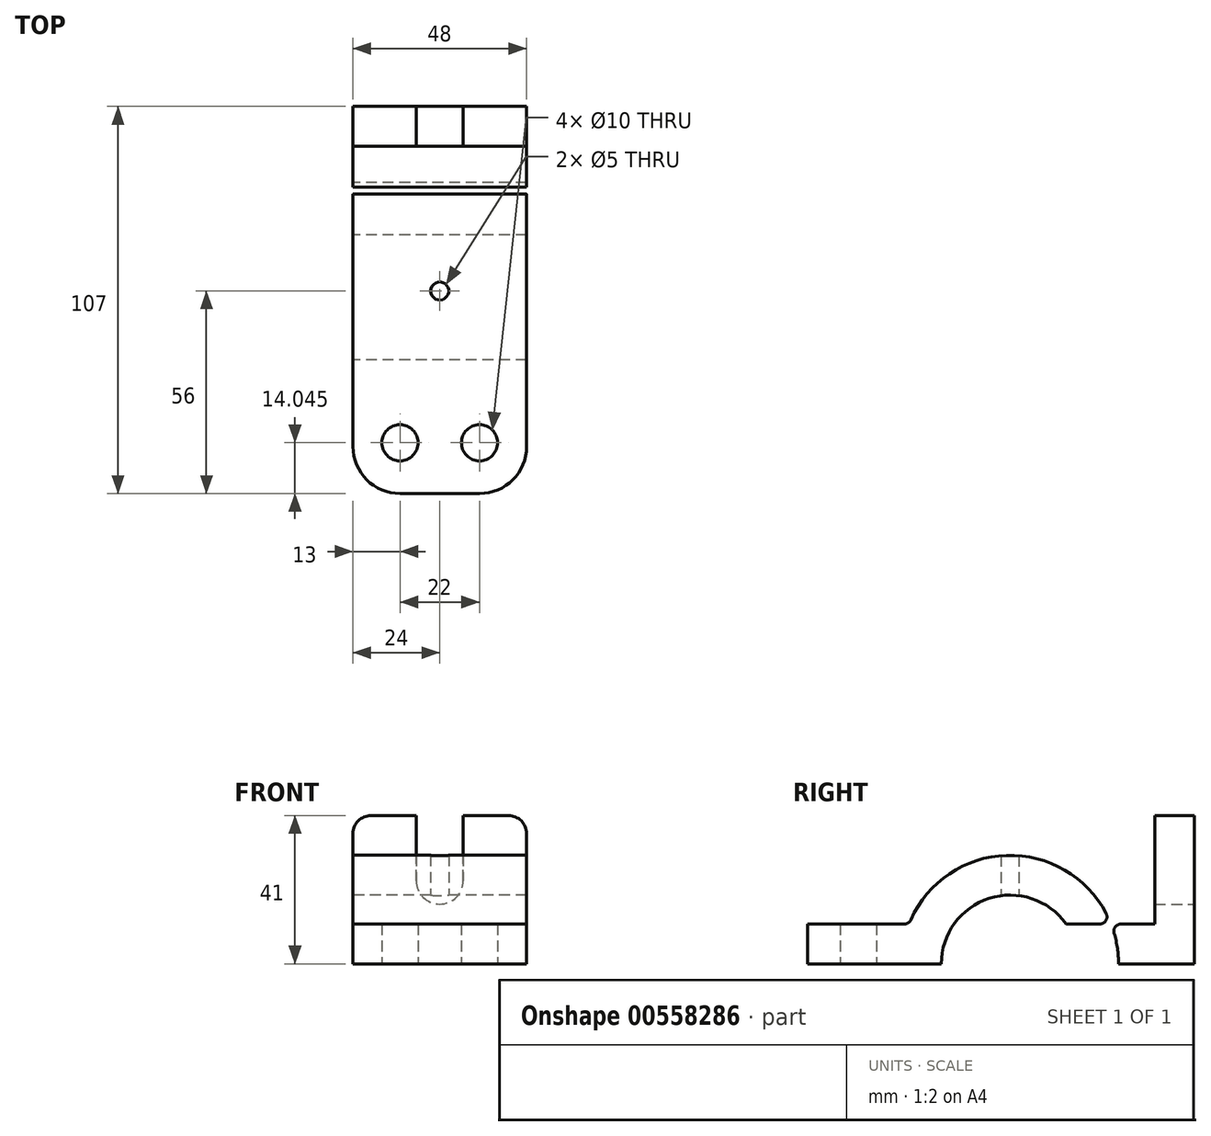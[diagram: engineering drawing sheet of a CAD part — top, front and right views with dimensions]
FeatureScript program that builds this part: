
annotation { "Feature Type Name" : "Feature", "Feature Type Description" : "" }
export const myFeature = defineFeature(function(context is Context, id is Id, definition is map)
    precondition{}
    {
        {
            var Q0;
            Q0=qCreatedBy(makeId("Right.planeOp"),FACE);
            var sketch = newSketch(context, id + "F0", { "sketchPlane" : qUnion([Q0])});
            skCircle(sketch, "E0", {"center": v(0, 0) * mm, "radius": 19 * mm});
            skCircle(sketch, "E1", {"center": v(0, 0) * mm, "radius": 30 * mm});
            skLineSegment(sketch, "E2.bottom", {"start": v(-56, 0) * mm, "end": v(51, 0) * mm});
            skLineSegment(sketch, "E2.top", {"start": v(-56, 11) * mm, "end": v(51, 11) * mm});
            skLineSegment(sketch, "E2.left", {"start": v(-56, 0) * mm, "end": v(-56, 11) * mm});
            skLineSegment(sketch, "E2.right", {"start": v(51, 0) * mm, "end": v(51, 11) * mm});
            skLineSegment(sketch, "E3.bottom", {"start": v(51, 41) * mm, "end": v(40, 41) * mm});
            skLineSegment(sketch, "E3.top", {"start": v(51, 11) * mm, "end": v(40, 11) * mm});
            skLineSegment(sketch, "E3.left", {"start": v(51, 41) * mm, "end": v(51, 11) * mm});
            skLineSegment(sketch, "E3.right", {"start": v(40, 41) * mm, "end": v(40, 11) * mm});
            skSolve(sketch);
        }
        {
            var Q0;
            Q0=makeQuery(id+"F0.imprint","IMPRINT",FACE,{"disambiguationData":[TD([[makeQuery(id+"F0.imprint","IMPRINT",EDGE,{"derivedFrom":sQuery(id+"F0.wireOp",EDGE,"E3.bottom")}),1.0]])]});
            var Q1;
            {var subQ4=sQuery(id+"F0.wireOp",EDGE,"E2.right");Q1=makeQuery(id+"F0.imprint","IMPRINT",FACE,{"disambiguationData":[TD([[makeQuery(id+"F0.imprint","IMPRINT",EDGE,{"derivedFrom":subQ4}),1.0]])]});}
            var Q2;
            {var subQ0=sQuery(id+"F0.wireOp",EDGE,"E2.top");var subQ1=sQuery(id+"F0.wireOp",EDGE,"E0");var subQ2=makeQuery(id+"F0.imprint","INTERSECT",VERTEX,{"disambiguationData":[OD(0.0)],"derivedFrom":[subQ1,subQ0]});Q2=makeQuery(id+"F0.imprint","IMPRINT",FACE,{"disambiguationData":[TD([[makeQuery(id+"F0.imprint","IMPRINT",EDGE,{"disambiguationData":[TD([[subQ2,-1.0]])],"derivedFrom":subQ1}),-1.0]])]});}
            var Q3;
            {var subQ0=sQuery(id+"F0.wireOp",EDGE,"E2.top");var subQ1=sQuery(id+"F0.wireOp",EDGE,"E0");var subQ2=makeQuery(id+"F0.imprint","INTERSECT",VERTEX,{"disambiguationData":[OD(0.0)],"derivedFrom":[subQ1,subQ0]});Q3=makeQuery(id+"F0.imprint","IMPRINT",FACE,{"disambiguationData":[TD([[makeQuery(id+"F0.imprint","IMPRINT",EDGE,{"disambiguationData":[TD([[subQ2,1.0]])],"derivedFrom":subQ1}),-1.0]])]});}
            var Q4;
            {var subQ0=sQuery(id+"F0.wireOp",EDGE,"E2.top");var subQ1=sQuery(id+"F0.wireOp",EDGE,"E0");var subQ2=makeQuery(id+"F0.imprint","INTERSECT",VERTEX,{"disambiguationData":[OD(1.0)],"derivedFrom":[subQ1,subQ0]});Q4=makeQuery(id+"F0.imprint","IMPRINT",FACE,{"disambiguationData":[TD([[makeQuery(id+"F0.imprint","IMPRINT",EDGE,{"disambiguationData":[TD([[subQ2,-1.0]])],"derivedFrom":subQ1}),-1.0]])]});}
            var Q5;
            {var subQ5=sQuery(id+"F0.wireOp",EDGE,"E2.left");Q5=makeQuery(id+"F0.imprint","IMPRINT",FACE,{"disambiguationData":[TD([[makeQuery(id+"F0.imprint","IMPRINT",EDGE,{"derivedFrom":subQ5}),-1.0]])]});}
            extrude(context, id + "F1", {"entities" : qUnion([Q0, Q1, Q2, Q3, Q4, Q5]), "endBound" : BoundingType.SYMMETRIC, "depth" : 48 * mm, "offsetDistance" : 25 * mm});
        }
        {
            var Q0;
            Q0=makeQuery(id+"F1.opExtrude","SWEPT_FACE",FACE,{"disambiguationData":[OSD([sQuery(id+"F0.wireOp",EDGE,"E2.right"),sQuery(id+"F0.wireOp",EDGE,"E3.left")])]});
            var sketch = newSketch(context, id + "F2", { "sketchPlane" : qUnion([Q0])});
            skLineSegment(sketch, "E4", {"start": v(0, 0) * mm, "end": v(0, 41) * mm});
            skCircle(sketch, "E5", {"center": v(0, 23) * mm, "radius": 6.5 * mm});
            skLineSegment(sketch, "E6", {"start": v(-6.5, 23) * mm, "end": v(-6.5, 41) * mm});
            skLineSegment(sketch, "E7", {"start": v(6.5, 23) * mm, "end": v(6.5, 41) * mm});
            skSolve(sketch);
        }
        {
            var Q0;
            {var subQ5=sQuery(id+"F2.wireOp",EDGE,"E6");Q0=makeQuery(id+"F2.imprint","IMPRINT",FACE,{"disambiguationData":[TD([[makeQuery(id+"F2.imprint","IMPRINT",EDGE,{"derivedFrom":subQ5}),-1.0]])]});}
            var Q1;
            {var subQ0=sQuery(id+"F2.wireOp",EDGE,"E5");var subQ1=sQuery(id+"F2.wireOp",EDGE,"E4");var subQ2=makeQuery(id+"F2.imprint","INTERSECT",VERTEX,{"disambiguationData":[OD(0.0)],"derivedFrom":[subQ1,subQ0]});Q1=makeQuery(id+"F2.imprint","IMPRINT",FACE,{"disambiguationData":[TD([[makeQuery(id+"F2.imprint","IMPRINT",EDGE,{"disambiguationData":[TD([[subQ2,-1.0]])],"derivedFrom":subQ1}),1.0]])]});}
            var Q2;
            {var subQ0=sQuery(id+"F2.wireOp",EDGE,"E5");var subQ1=sQuery(id+"F2.wireOp",EDGE,"E4");var subQ2=makeQuery(id+"F2.imprint","INTERSECT",VERTEX,{"disambiguationData":[OD(0.0)],"derivedFrom":[subQ1,subQ0]});Q2=makeQuery(id+"F2.imprint","IMPRINT",FACE,{"disambiguationData":[TD([[makeQuery(id+"F2.imprint","IMPRINT",EDGE,{"disambiguationData":[TD([[subQ2,-1.0]])],"derivedFrom":subQ1}),-1.0]])]});}
            var Q3;
            {var subQ5=sQuery(id+"F2.wireOp",EDGE,"E7");Q3=makeQuery(id+"F2.imprint","IMPRINT",FACE,{"disambiguationData":[TD([[makeQuery(id+"F2.imprint","IMPRINT",EDGE,{"derivedFrom":subQ5}),1.0]])]});}
            var Q4;
            Q4=makeQuery(id+"F1.opExtrude","SWEPT_FACE",FACE,{"disambiguationData":[OSD([sQuery(id+"F0.wireOp",EDGE,"E3.right")])]});
            extrude(context, id + "F3", {"entities" : qUnion([Q0, Q1, Q2, Q3]), "operationType" : NewBodyOperationType.REMOVE, "endBound" : BoundingType.UP_TO_SURFACE, "oppositeDirection" : true, "depth" : 25 * mm, "endBoundEntityFace" : qUnion([Q4]), "offsetDistance" : 25 * mm});
        }
        {
            var Q0;
            Q0=qCreatedBy(makeId("Top.planeOp"),FACE);
            var sketch = newSketch(context, id + "F4", { "sketchPlane" : qUnion([Q0])});
            skCircle(sketch, "E8", {"center": v(0, 0) * mm, "radius": 2.5 * mm});
            skLineSegment(sketch, "E9", {"start": v(-24, -41.96) * mm, "end": v(24, -41.96) * mm, "construction": true});
            skLineSegment(sketch, "E10", {"start": v(0, -56) * mm, "end": v(0, -27.91) * mm, "construction": true});
            skCircle(sketch, "E11", {"center": v(-11, -41.96) * mm, "radius": 5 * mm});
            skCircle(sketch, "E12", {"center": v(11, -41.96) * mm, "radius": 5 * mm});
            skSolve(sketch);
        }
        {
            var Q0;
            Q0=makeQuery(id+"F4.imprint","IMPRINT",FACE,{"disambiguationData":[TD([[makeQuery(id+"F4.imprint","IMPRINT",EDGE,{"derivedFrom":sQuery(id+"F4.wireOp",EDGE,"E8")}),1.0]])]});
            var Q1;
            Q1=makeQuery(id+"F4.imprint","IMPRINT",FACE,{"disambiguationData":[TD([[makeQuery(id+"F4.imprint","IMPRINT",EDGE,{"derivedFrom":sQuery(id+"F4.wireOp",EDGE,"E12")}),1.0]])]});
            var Q2;
            Q2=makeQuery(id+"F4.imprint","IMPRINT",FACE,{"disambiguationData":[TD([[makeQuery(id+"F4.imprint","IMPRINT",EDGE,{"derivedFrom":sQuery(id+"F4.wireOp",EDGE,"E11")}),1.0]])]});
            extrude(context, id + "F5", {"entities" : qUnion([Q0, Q1, Q2]), "operationType" : NewBodyOperationType.REMOVE, "endBound" : BoundingType.THROUGH_ALL, "depth" : 25 * mm, "offsetDistance" : 25 * mm});
        }
        {
            var Q0;
            Q0=makeQuery(id+"F1.opExtrude","CAP_EDGE",EDGE,{"disambiguationData":[OSD([sQuery(id+"F0.wireOp",EDGE,"E2.left")])],"isStart":true});
            var Q1;
            Q1=makeQuery(id+"F1.opExtrude","CAP_EDGE",EDGE,{"disambiguationData":[OSD([sQuery(id+"F0.wireOp",EDGE,"E2.left")])],"isStart":false});
            fillet(context, id + "F6", {"entities" : qUnion([Q0, Q1]), "radius" : 13 * mm, "tangentPropagation" : true, "allowEdgeOverflow" : false});
        }
        {
            var Q0;
            Q0=makeQuery(id+"F1.opExtrude","CAP_EDGE",EDGE,{"disambiguationData":[OSD([sQuery(id+"F0.wireOp",EDGE,"E3.bottom")])],"isStart":true});
            var Q1;
            Q1=makeQuery(id+"F1.opExtrude","CAP_EDGE",EDGE,{"disambiguationData":[OSD([sQuery(id+"F0.wireOp",EDGE,"E3.bottom")])],"isStart":false});
            fillet(context, id + "F7", {"entities" : qUnion([Q0, Q1]), "radius" : 5 * mm, "tangentPropagation" : true, "allowEdgeOverflow" : false});
        }
        {
            var Q0;
            {var subQ0=sQuery(id+"F0.wireOp",EDGE,"E2.top");var subQ1=sQuery(id+"F0.wireOp",EDGE,"E1");Q0=makeQuery(id+"F1.opExtrude","SWEPT_EDGE",EDGE,{"disambiguationData":[OSD([subQ1,subQ0]),TDD([makeQuery(id+"F0.imprint","INTERSECT",VERTEX,{"disambiguationData":[OD(1.0)],"derivedFrom":[subQ1,subQ0]})])]});}
            var Q1;
            {var subQ0=sQuery(id+"F0.wireOp",EDGE,"E2.top");var subQ1=sQuery(id+"F0.wireOp",EDGE,"E1");Q1=makeQuery(id+"F1.opExtrude","SWEPT_EDGE",EDGE,{"disambiguationData":[OSD([subQ1,subQ0]),TDD([makeQuery(id+"F0.imprint","INTERSECT",VERTEX,{"disambiguationData":[OD(0.0)],"derivedFrom":[subQ1,subQ0]})])]});}
            fillet(context, id + "F8", {"entities" : qUnion([Q0, Q1]), "radius" : 2 * mm, "tangentPropagation" : true, "allowEdgeOverflow" : false});
        }
    });
